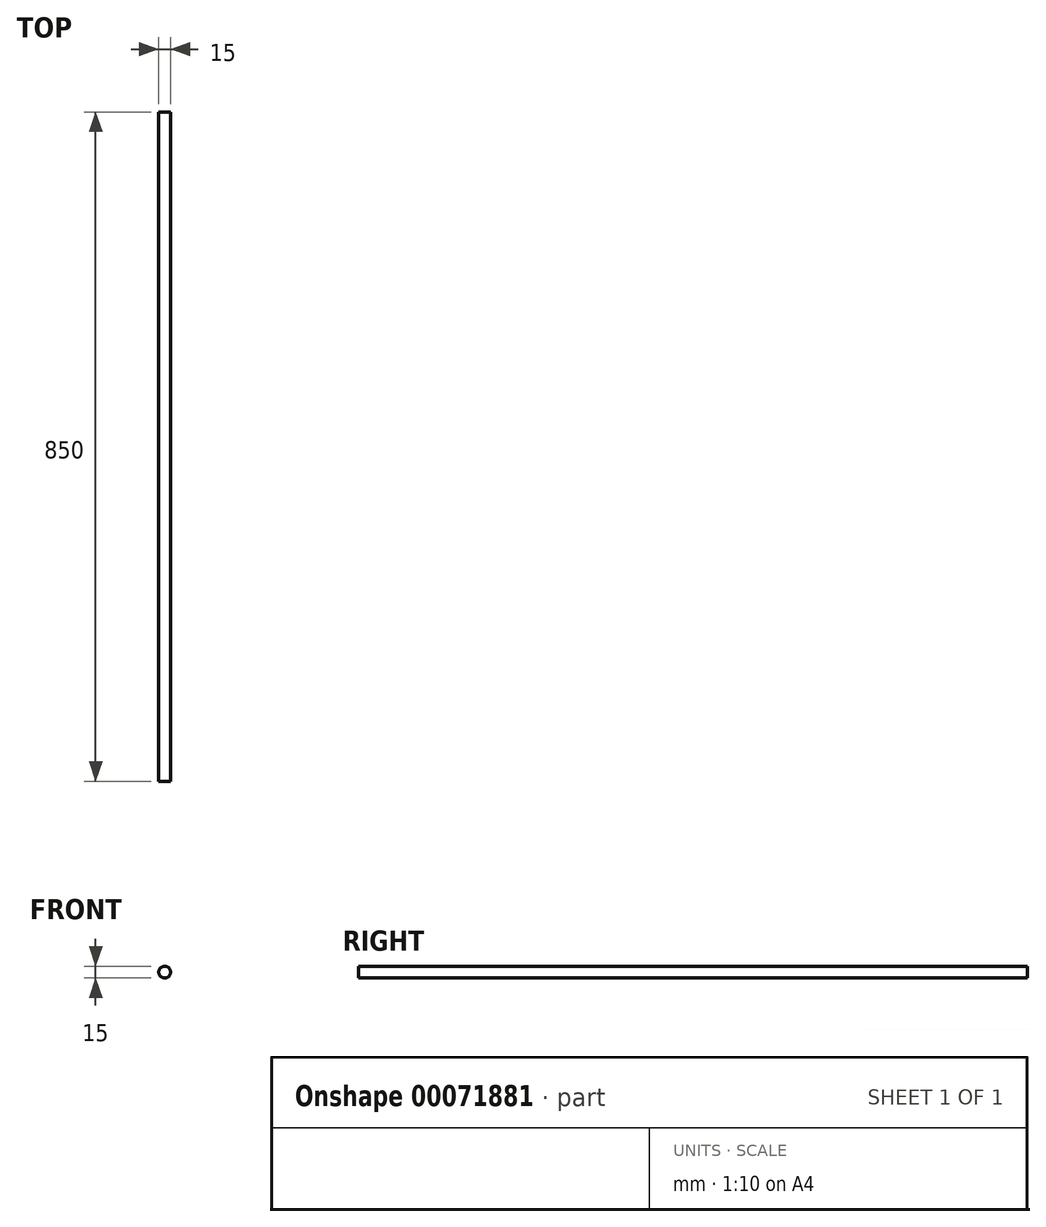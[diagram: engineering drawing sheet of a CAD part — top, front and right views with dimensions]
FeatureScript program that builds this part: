
annotation { "Feature Type Name" : "Feature", "Feature Type Description" : "" }
export const myFeature = defineFeature(function(context is Context, id is Id, definition is map)
    precondition{}
    {
        {
            var Q0;
            Q0=qCreatedBy(makeId("Front.planeOp"),FACE);
            var sketch = newSketch(context, id + "F0", { "sketchPlane" : qUnion([Q0])});
            skCircle(sketch, "E0", {"center": v(0, 0) * mm, "radius": 7.5 * mm});
            skSolve(sketch);
        }
        {
            var Q0;
            Q0=makeQuery(id+"F0.imprint","IMPRINT",FACE,{"disambiguationData":[TD([[makeQuery(id+"F0.imprint","IMPRINT",EDGE,{"derivedFrom":sQuery(id+"F0.wireOp",EDGE,"E0")}),1.0]])]});
            extrude(context, id + "F1", {"entities" : qUnion([Q0]), "oppositeDirection" : true, "depth" : 850 * mm});
        }
    });
